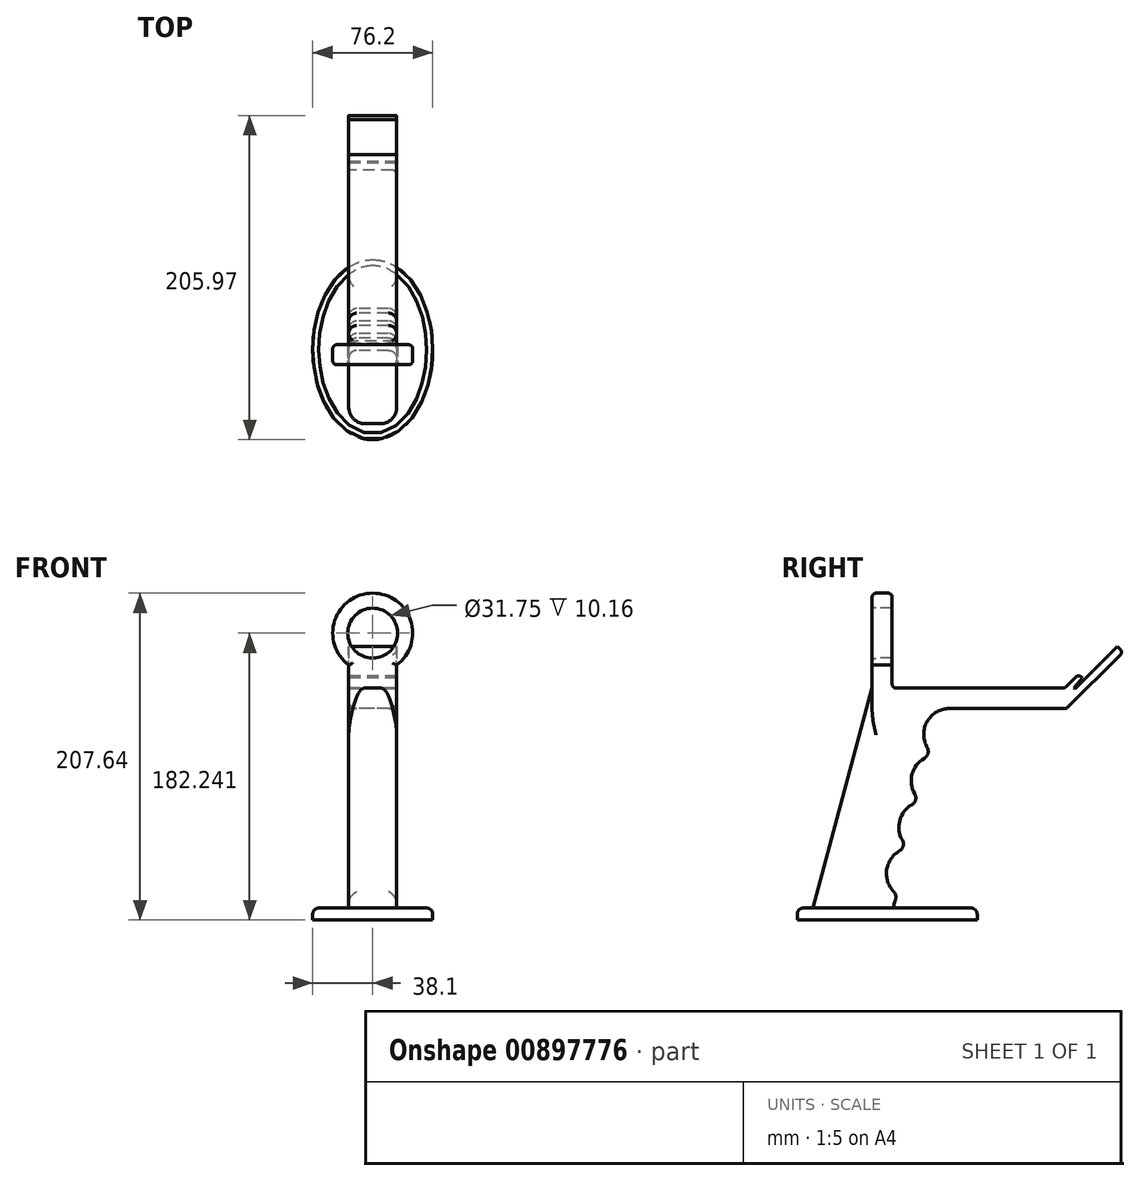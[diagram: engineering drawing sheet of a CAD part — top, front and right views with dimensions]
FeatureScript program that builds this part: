
annotation { "Feature Type Name" : "Feature", "Feature Type Description" : "" }
export const myFeature = defineFeature(function(context is Context, id is Id, definition is map)
    precondition{}
    {
        {
            var Q0;
            Q0=qCreatedBy(makeId("Right.planeOp"),FACE);
            var sketch = newSketch(context, id + "F0", { "sketchPlane" : qUnion([Q0])});
            skLineSegment(sketch, "E0", {"start": v(0, 0) * mm, "end": v(37.43, 139.7) * mm});
            skLineSegment(sketch, "E1", {"start": v(50.13, 139.7) * mm, "end": v(159.62, 139.7) * mm});
            skLineSegment(sketch, "E2", {"start": v(50.8, 0) * mm, "end": v(0, 0) * mm});
            skLineSegment(sketch, "E3", {"start": v(94.58, 139.7) * mm, "end": v(57.15, 0) * mm, "construction": true});
            skArc(sketch, "E4", {"start": v(84.74, 126.65) * mm, "mid": v(70.75, 114.53) * mm, "end": v(76.8, 97.04) * mm});
            skArc(sketch, "E5", {"start": v(76.85, 97.21) * mm, "mid": v(62.86, 85.1) * mm, "end": v(68.91, 67.6) * mm});
            skArc(sketch, "E6", {"start": v(68.96, 67.77) * mm, "mid": v(54.97, 55.65) * mm, "end": v(61.02, 38.16) * mm});
            skArc(sketch, "E7", {"start": v(61.07, 38.33) * mm, "mid": v(47.08, 26.2) * mm, "end": v(53.14, 8.72) * mm});
            skLineSegment(sketch, "E8.trimOffspring", {"start": v(61.07, 38.33) * mm, "end": v(61.02, 38.16) * mm});
            skLineSegment(sketch, "E9.trimOffspring", {"start": v(68.96, 67.77) * mm, "end": v(68.91, 67.6) * mm});
            skLineSegment(sketch, "E10.trimOffspring", {"start": v(76.85, 97.21) * mm, "end": v(76.8, 97.04) * mm});
            skLineSegment(sketch, "E11.trimOffspring", {"start": v(53.14, 8.72) * mm, "end": v(50.8, 0) * mm});
            skLineSegment(sketch, "E12", {"start": v(84.74, 126.65) * mm, "end": v(160.94, 126.65) * mm});
            skLineSegment(sketch, "E13", {"start": v(160.94, 126.65) * mm, "end": v(196.86, 162.57) * mm});
            skLineSegment(sketch, "E14", {"start": v(168.49, 148.57) * mm, "end": v(159.62, 139.7) * mm});
            skLineSegment(sketch, "E15", {"start": v(37.43, 139.7) * mm, "end": v(37.43, 149.86) * mm});
            skLineSegment(sketch, "E16", {"start": v(37.43, 149.86) * mm, "end": v(50.13, 149.86) * mm});
            skLineSegment(sketch, "E17", {"start": v(50.13, 149.86) * mm, "end": v(50.13, 139.7) * mm});
            skLineSegment(sketch, "E18", {"start": v(196.86, 162.57) * mm, "end": v(193.27, 166.17) * mm});
            skLineSegment(sketch, "E19", {"start": v(193.27, 166.17) * mm, "end": v(166.32, 139.22) * mm});
            skLineSegment(sketch, "E20", {"start": v(166.32, 139.22) * mm, "end": v(165.6, 139.94) * mm});
            skLineSegment(sketch, "E21", {"start": v(165.6, 139.94) * mm, "end": v(171, 146.06) * mm});
            skLineSegment(sketch, "E22", {"start": v(171, 146.06) * mm, "end": v(168.49, 148.57) * mm});
            skSolve(sketch);
        }
        {
            var Q0;
            Q0=makeQuery(id+"F0.imprint","IMPRINT",FACE,{"disambiguationData":[TD([[makeQuery(id+"F0.imprint","IMPRINT",EDGE,{"derivedFrom":sQuery(id+"F0.wireOp",EDGE,"E0")}),-1.0]])]});
            extrude(context, id + "F1", {"entities" : qUnion([Q0]), "depth" : 30.48 * mm, "offsetDistance" : 25.4 * mm});
        }
        {
            var Q0;
            Q0=makeQuery(id+"F1.opExtrude","CAP_EDGE",EDGE,{"disambiguationData":[OSD([sQuery(id+"F0.wireOp",EDGE,"E4")])],"isStart":false});
            var Q1;
            Q1=makeQuery(id+"F1.opExtrude","CAP_EDGE",EDGE,{"disambiguationData":[OSD([sQuery(id+"F0.wireOp",EDGE,"E5")])],"isStart":false});
            var Q2;
            Q2=makeQuery(id+"F1.opExtrude","CAP_EDGE",EDGE,{"disambiguationData":[OSD([sQuery(id+"F0.wireOp",EDGE,"E6")])],"isStart":false});
            var Q3;
            Q3=makeQuery(id+"F1.opExtrude","CAP_EDGE",EDGE,{"disambiguationData":[OSD([sQuery(id+"F0.wireOp",EDGE,"E7")])],"isStart":false});
            var Q4;
            Q4=makeQuery(id+"F1.opExtrude","CAP_EDGE",EDGE,{"disambiguationData":[OSD([sQuery(id+"F0.wireOp",EDGE,"E7")])],"isStart":true});
            var Q5;
            Q5=makeQuery(id+"F1.opExtrude","CAP_EDGE",EDGE,{"disambiguationData":[OSD([sQuery(id+"F0.wireOp",EDGE,"E6")])],"isStart":true});
            var Q6;
            Q6=makeQuery(id+"F1.opExtrude","CAP_EDGE",EDGE,{"disambiguationData":[OSD([sQuery(id+"F0.wireOp",EDGE,"E5")])],"isStart":true});
            var Q7;
            Q7=makeQuery(id+"F1.opExtrude","CAP_EDGE",EDGE,{"disambiguationData":[OSD([sQuery(id+"F0.wireOp",EDGE,"E4")])],"isStart":true});
            var Q8;
            Q8=makeQuery(id+"F1.opExtrude","SWEPT_EDGE",EDGE,{"disambiguationData":[OSD([sQuery(id+"F0.wireOp",EDGE,"E4"),sQuery(id+"F0.wireOp",EDGE,"E5")])]});
            var Q9;
            Q9=makeQuery(id+"F1.opExtrude","SWEPT_EDGE",EDGE,{"disambiguationData":[OSD([sQuery(id+"F0.wireOp",EDGE,"E5"),sQuery(id+"F0.wireOp",EDGE,"E6")])]});
            var Q10;
            Q10=makeQuery(id+"F1.opExtrude","SWEPT_EDGE",EDGE,{"disambiguationData":[OSD([sQuery(id+"F0.wireOp",EDGE,"E6"),sQuery(id+"F0.wireOp",EDGE,"E7")])]});
            var Q11;
            Q11=makeQuery(id+"F1.opExtrude","SWEPT_EDGE",EDGE,{"disambiguationData":[OSD([sQuery(id+"F0.wireOp",EDGE,"E7"),sQuery(id+"F0.wireOp",EDGE,"E11.trimOffspring")])]});
            var Q12;
            Q12=makeQuery(id+"F1.opExtrude","SWEPT_EDGE",EDGE,{"disambiguationData":[OSD([sQuery(id+"F0.wireOp",EDGE,"TelIYqah-B2Uh-ikoH-394u-6YLBrA3NFfos"),sQuery(id+"F0.wireOp",EDGE,"E4")])]});
            fillet(context, id + "F2", {"entities" : qUnion([Q0, Q1, Q2, Q3, Q4, Q5, Q6, Q7, Q8, Q9, Q10, Q11, Q12]), "radius" : 5.08 * mm, "tangentPropagation" : true, "allowEdgeOverflow" : false});
        }
        {
            var Q0;
            Q0=makeQuery(id+"F1.opExtrude","SWEPT_FACE",FACE,{"disambiguationData":[OSD([sQuery(id+"F0.wireOp",EDGE,"E2")])]});
            var sketch = newSketch(context, id + "F3", { "sketchPlane" : qUnion([Q0])});
            skLineSegment(sketch, "E23", {"start": v(15.24, 0) * mm, "end": v(15.24, -50.8) * mm, "construction": true});
            skEllipse(sketch, "E24", {"center": v(15.24, -47) * mm, "majorRadius": 57.15 * mm, "minorRadius": 38.1 * mm, "majorAxis": v(0, -1)});
            skSolve(sketch);
        }
        {
            var Q0;
            Q0 = qSketchRegion(id + "F3", true);
            extrude(context, id + "F4", {"entities" : qUnion([Q0]), "operationType" : NewBodyOperationType.ADD, "depth" : 7.62 * mm, "offsetDistance" : 25.4 * mm});
        }
        {
            var Q0;
            Q0=makeQuery(id+"F1.opExtrude","CAP_EDGE",EDGE,{"disambiguationData":[OSD([sQuery(id+"F0.wireOp",EDGE,"E0")])],"isStart":true});
            var Q1;
            Q1=makeQuery(id+"F1.opExtrude","CAP_EDGE",EDGE,{"disambiguationData":[OSD([sQuery(id+"F0.wireOp",EDGE,"E0")])],"isStart":false});
            fillet(context, id + "F5", {"entities" : qUnion([Q0, Q1]), "radius" : 10.16 * mm, "tangentPropagation" : true, "allowEdgeOverflow" : false});
        }
        {
            var Q0;
            {var subQ0=sQuery(id+"F0.wireOp",EDGE,"E0");var subQ1=sQuery(id+"F0.wireOp",EDGE,"E2");var subQ3=sQuery(id+"F3.wireOp",EDGE,"E24");var subQ4=makeQuery(id+"F4.opExtrude","SWEPT_FACE",FACE,{"disambiguationData":[OSD([subQ3])]});var subQ5=makeQuery(id+"F4.opExtrude","CAP_FACE",FACE,{"disambiguationData":[OSD([subQ3])],"isStart":true});var subQ6=makeQuery(id+"F4.opExtrude","CAP_EDGE",EDGE,{"disambiguationData":[OSD([subQ3])],"isStart":true});var subQ7=sQuery(id+"F0.wireOp",EDGE,"E11.trimOffspring");var subQ8=sQuery(id+"F0.wireOp",EDGE,"E7");var subQ9=sQuery(id+"F0.wireOp",EDGE,"E6");var subQ10=sQuery(id+"F0.wireOp",EDGE,"E5");var subQ11=sQuery(id+"F0.wireOp",EDGE,"E4");var subQ12=sQuery(id+"F0.wireOp",EDGE,"TelIYqah-B2Uh-ikoH-394u-6YLBrA3NFfos");var subQ13=sQuery(id+"F0.wireOp",EDGE,"E1");Q0=makeQuery(id+"F5.opFillet","MERGE",EDGE,{"derivedFrom":[makeQuery(id+"F4.boolean.opBoolean","SPLIT",EDGE,{"disambiguationData":[topologyDisambiguationEdgeConnected([subQ4,subQ5]),TD([makeQuery(id+"F1.opExtrude","CAP_FACE",FACE,{"disambiguationData":[OSD([subQ0,subQ13,subQ12,subQ1,subQ11,subQ10,subQ9,subQ8,subQ7])],"isStart":true})])],"derivedFrom":subQ6}),makeQuery(id+"F4.boolean.opBoolean","SPLIT",EDGE,{"disambiguationData":[topologyDisambiguationEdgeConnected([subQ4,subQ5]),TD([makeQuery(id+"F1.opExtrude","SWEPT_FACE",FACE,{"disambiguationData":[OSD([subQ0])]})])],"derivedFrom":subQ6})]});}
            fillet(context, id + "F6", {"entities" : qUnion([Q0]), "radius" : 3.8 * mm, "tangentPropagation" : true, "allowEdgeOverflow" : false});
        }
        {
            var Q0;
            Q0=makeQuery(id+"F1.opExtrude","SWEPT_FACE",FACE,{"disambiguationData":[OSD([sQuery(id+"F0.wireOp",EDGE,"E15")])]});
            var sketch = newSketch(context, id + "F7", { "sketchPlane" : qUnion([Q0])});
            skArc(sketch, "E25", {"start": v(30.48, 154.3) * mm, "mid": v(15.24, 200.02) * mm, "end": v(0, 154.3) * mm});
            skLineSegment(sketch, "E26", {"start": v(15.24, 149.86) * mm, "end": v(15.24, 214.23) * mm, "construction": true});
            skCircle(sketch, "E27", {"center": v(15.24, 174.62) * mm, "radius": 15.88 * mm});
            skLineSegment(sketch, "E28", {"start": v(0, 149.86) * mm, "end": v(0, 154.3) * mm});
            skLineSegment(sketch, "E29", {"start": v(30.48, 149.86) * mm, "end": v(30.48, 154.3) * mm});
            skLineSegment(sketch, "E30", {"start": v(0, 149.86) * mm, "end": v(30.48, 149.86) * mm});
            skSolve(sketch);
        }
        {
            var Q0;
            Q0 = qSketchRegion(id + "F7", true);
            extrude(context, id + "F8", {"entities" : qUnion([Q0]), "operationType" : NewBodyOperationType.ADD, "oppositeDirection" : true, "depth" : 12.7 * mm, "offsetDistance" : 25.4 * mm});
        }
        {
            var Q0;
            Q0=makeQuery(id+"F8.opExtrude","CAP_EDGE",EDGE,{"disambiguationData":[OSD([sQuery(id+"F7.wireOp",EDGE,"E25")])],"isStart":true});
            var Q1;
            Q1=makeQuery(id+"F8.boolean.opBoolean","MERGE",EDGE,{"derivedFrom":[makeQuery(id+"F1.opExtrude","CAP_EDGE",EDGE,{"disambiguationData":[OSD([sQuery(id+"F0.wireOp",EDGE,"E15")])],"isStart":true}),makeQuery(id+"F8.opExtrude","CAP_EDGE",EDGE,{"disambiguationData":[OSD([sQuery(id+"F7.wireOp",EDGE,"E28")])],"isStart":true})]});
            var Q2;
            Q2=makeQuery(id+"F8.boolean.opBoolean","MERGE",EDGE,{"derivedFrom":[makeQuery(id+"F1.opExtrude","CAP_EDGE",EDGE,{"disambiguationData":[OSD([sQuery(id+"F0.wireOp",EDGE,"E15")])],"isStart":false}),makeQuery(id+"F8.opExtrude","CAP_EDGE",EDGE,{"disambiguationData":[OSD([sQuery(id+"F7.wireOp",EDGE,"E29")])],"isStart":true})]});
            var Q3;
            Q3=makeQuery(id+"F8.boolean.opBoolean","MERGE",EDGE,{"derivedFrom":[makeQuery(id+"F1.opExtrude","CAP_EDGE",EDGE,{"disambiguationData":[OSD([sQuery(id+"F0.wireOp",EDGE,"E17")])],"isStart":false}),makeQuery(id+"F8.opExtrude","CAP_EDGE",EDGE,{"disambiguationData":[OSD([sQuery(id+"F7.wireOp",EDGE,"E29")])],"isStart":false})]});
            var Q4;
            Q4=makeQuery(id+"F8.opExtrude","CAP_EDGE",EDGE,{"disambiguationData":[OSD([sQuery(id+"F7.wireOp",EDGE,"E27")])],"isStart":true});
            var Q5;
            Q5=makeQuery(id+"F8.opExtrude","CAP_EDGE",EDGE,{"disambiguationData":[OSD([sQuery(id+"F7.wireOp",EDGE,"E25")])],"isStart":false});
            var Q6;
            Q6=makeQuery(id+"F8.boolean.opBoolean","MERGE",EDGE,{"derivedFrom":[makeQuery(id+"F1.opExtrude","CAP_EDGE",EDGE,{"disambiguationData":[OSD([sQuery(id+"F0.wireOp",EDGE,"E17")])],"isStart":true}),makeQuery(id+"F8.opExtrude","CAP_EDGE",EDGE,{"disambiguationData":[OSD([sQuery(id+"F7.wireOp",EDGE,"E28")])],"isStart":false})]});
            var Q7;
            Q7=makeQuery(id+"F1.opExtrude","SWEPT_EDGE",EDGE,{"disambiguationData":[OSD([sQuery(id+"F0.wireOp",EDGE,"E1"),sQuery(id+"F0.wireOp",EDGE,"E17")])]});
            var Q8;
            Q8=makeQuery(id+"F1.opExtrude","SWEPT_EDGE",EDGE,{"disambiguationData":[OSD([sQuery(id+"F0.wireOp",EDGE,"E1"),sQuery(id+"F0.wireOp",EDGE,"E14")])]});
            var Q9;
            Q9=makeQuery(id+"F1.opExtrude","SWEPT_EDGE",EDGE,{"disambiguationData":[OSD([sQuery(id+"F0.wireOp",EDGE,"E13"),sQuery(id+"F0.wireOp",EDGE,"E18")])]});
            var Q10;
            Q10=makeQuery(id+"F1.opExtrude","CAP_EDGE",EDGE,{"disambiguationData":[OSD([sQuery(id+"F0.wireOp",EDGE,"E13")])],"isStart":false});
            var Q11;
            Q11=makeQuery(id+"F1.opExtrude","SWEPT_EDGE",EDGE,{"disambiguationData":[OSD([sQuery(id+"F0.wireOp",EDGE,"E14"),sQuery(id+"F0.wireOp",EDGE,"E22")])]});
            fillet(context, id + "F9", {"entities" : qUnion([Q0, Q1, Q2, Q3, Q4, Q5, Q6, Q7, Q8, Q9, Q10, Q11]), "radius" : 2.54 * mm, "tangentPropagation" : true, "allowEdgeOverflow" : false});
        }
    });
